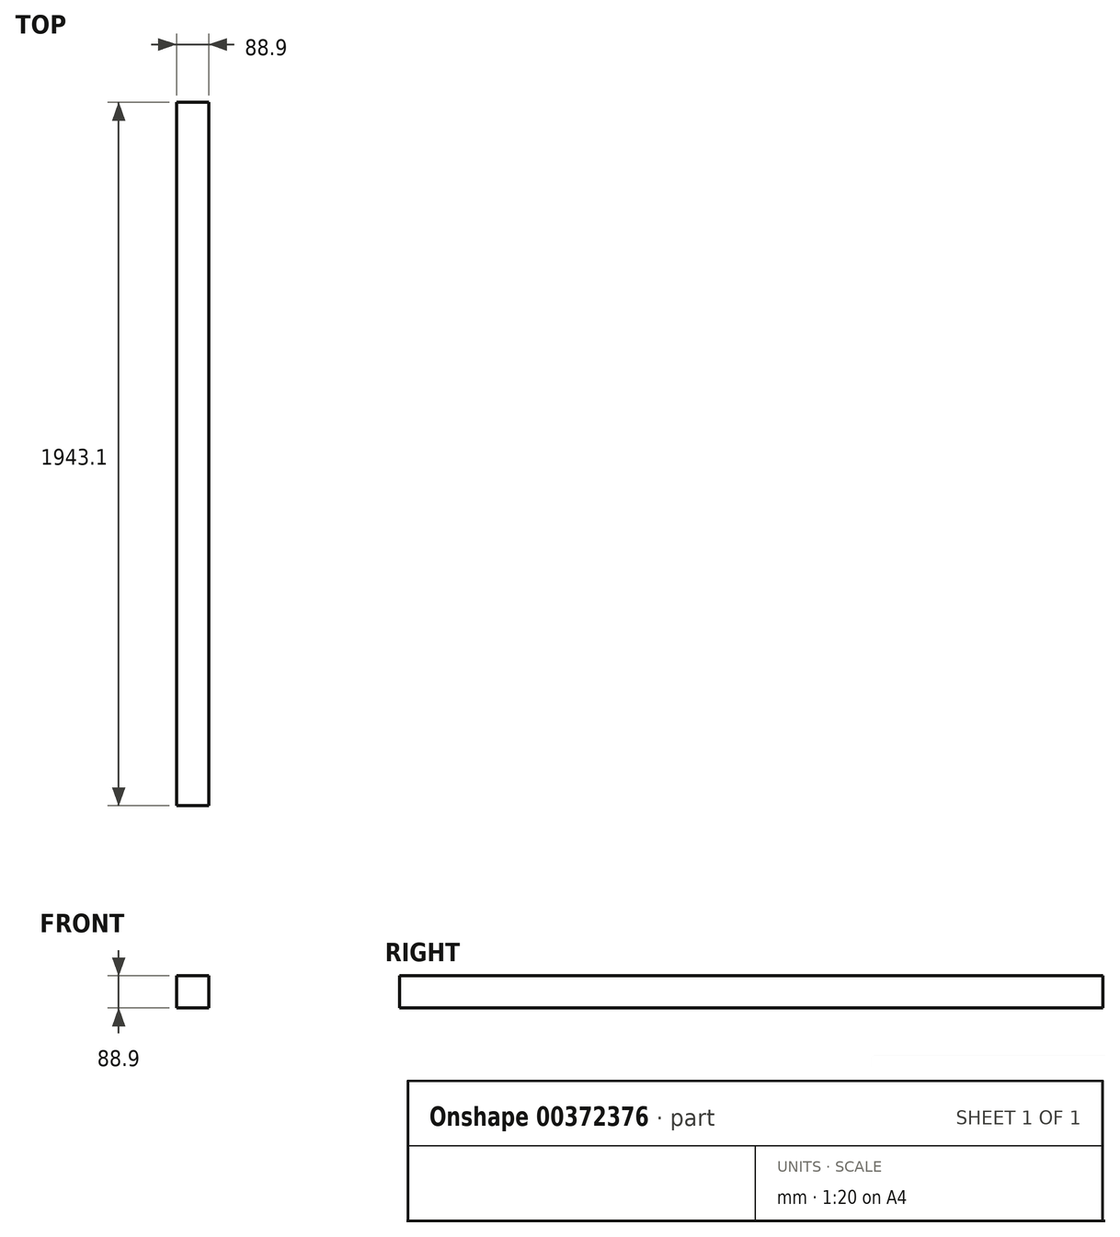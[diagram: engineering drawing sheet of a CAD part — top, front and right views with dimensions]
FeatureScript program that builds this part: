
annotation { "Feature Type Name" : "Feature", "Feature Type Description" : "" }
export const myFeature = defineFeature(function(context is Context, id is Id, definition is map)
    precondition{}
    {
        {
            var Q0;
            Q0=qCreatedBy(makeId("Front.planeOp"),FACE);
            var sketch = newSketch(context, id + "F0", { "sketchPlane" : qUnion([Q0])});
            skLineSegment(sketch, "E0.bottom", {"start": v(-44.45, 44.45) * mm, "end": v(44.45, 44.45) * mm});
            skLineSegment(sketch, "E0.top", {"start": v(-44.45, -44.45) * mm, "end": v(44.45, -44.45) * mm});
            skLineSegment(sketch, "E0.left", {"start": v(-44.45, 44.45) * mm, "end": v(-44.45, -44.45) * mm});
            skLineSegment(sketch, "E0.right", {"start": v(44.45, 44.45) * mm, "end": v(44.45, -44.45) * mm});
            skPoint(sketch, "E0.middle", {"position": v(0, 0) * mm});
            skSolve(sketch);
        }
        {
            var Q0;
            Q0 = qSketchRegion(id + "F0", true);
            extrude(context, id + "F1", {"entities" : qUnion([Q0]), "endBound" : BoundingType.SYMMETRIC, "oppositeDirection" : true, "depth" : 1943.1 * mm});
        }
    });
